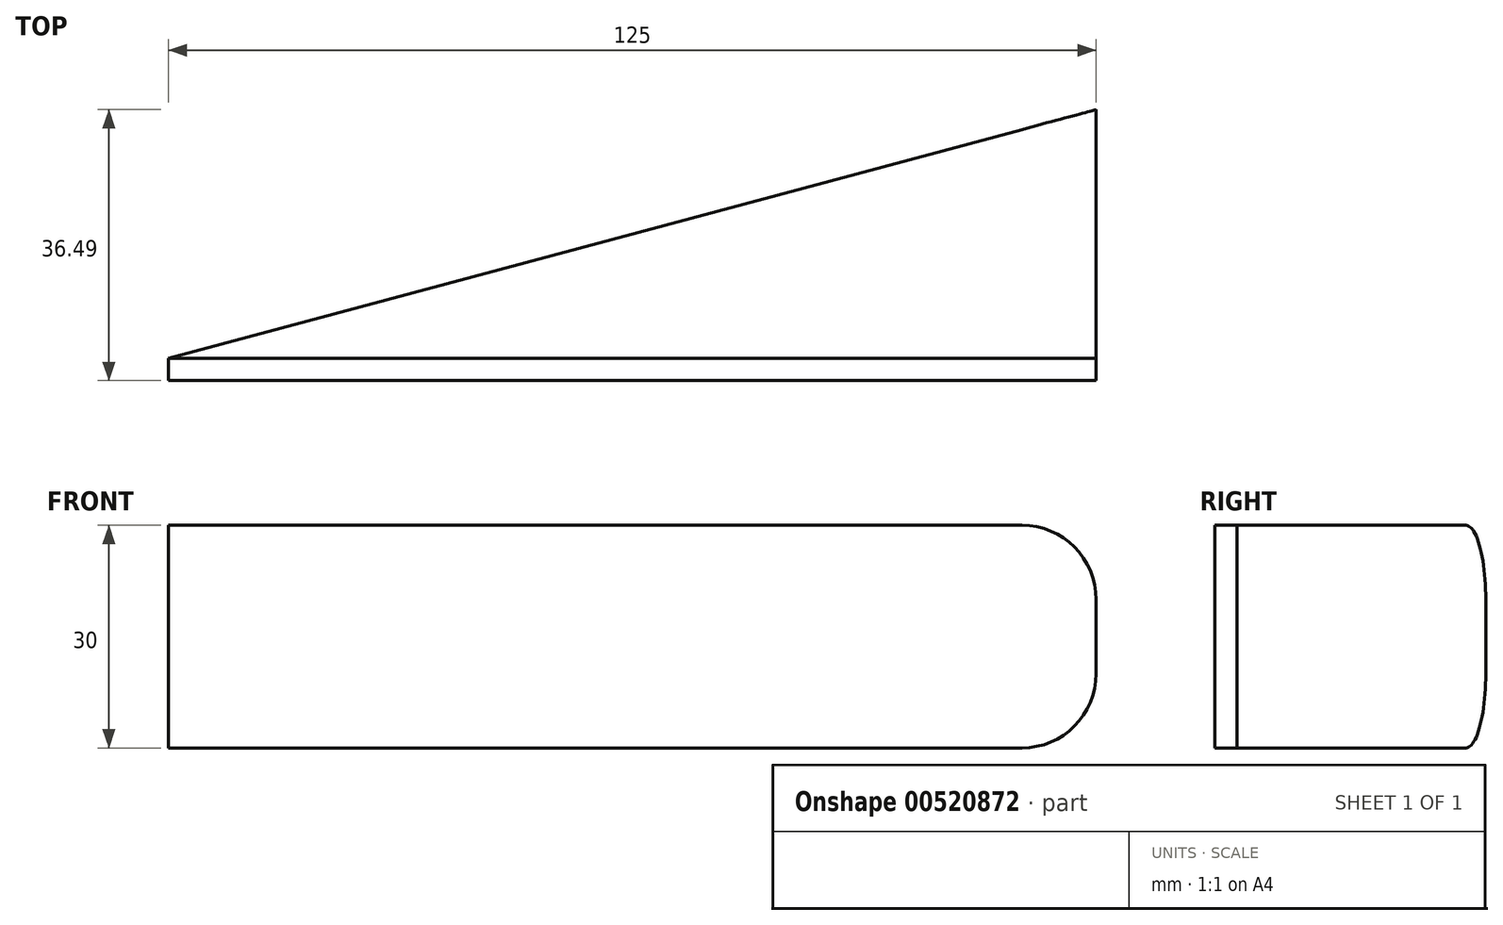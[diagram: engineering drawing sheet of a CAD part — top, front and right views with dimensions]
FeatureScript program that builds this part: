
annotation { "Feature Type Name" : "Feature", "Feature Type Description" : "" }
export const myFeature = defineFeature(function(context is Context, id is Id, definition is map)
    precondition{}
    {
        {
            var Q0;
            Q0=qCreatedBy(makeId("Top.planeOp"),FACE);
            var sketch = newSketch(context, id + "F0", { "sketchPlane" : qUnion([Q0])});
            skLineSegment(sketch, "E0", {"start": v(0, 0) * mm, "end": v(125, 0) * mm});
            skLineSegment(sketch, "E1", {"start": v(125, 0) * mm, "end": v(125, 33.5) * mm});
            skLineSegment(sketch, "E2", {"start": v(125, 33.5) * mm, "end": v(0, 0) * mm});
            skLineSegment(sketch, "E3.top", {"start": v(0, -3) * mm, "end": v(125, -3) * mm});
            skLineSegment(sketch, "E3.left", {"start": v(0, 0) * mm, "end": v(0, -3) * mm});
            skLineSegment(sketch, "E3.right", {"start": v(125, 0) * mm, "end": v(125, -3) * mm});
            skSolve(sketch);
        }
        {
            var Q0;
            Q0=makeQuery(id+"F0.imprint","IMPRINT",FACE,{"disambiguationData":[TD([[makeQuery(id+"F0.imprint","IMPRINT",EDGE,{"derivedFrom":sQuery(id+"F0.wireOp",EDGE,"E1")}),1.0]])]});
            extrude(context, id + "F1", {"entities" : qUnion([Q0]), "depth" : 30 * mm, "offsetDistance" : 25 * mm});
        }
        {
            var Q0;
            Q0=makeQuery(id+"F0.imprint","IMPRINT",FACE,{"disambiguationData":[TD([[makeQuery(id+"F0.imprint","IMPRINT",EDGE,{"derivedFrom":sQuery(id+"F0.wireOp",EDGE,"E0")}),-1.0]])]});
            extrude(context, id + "F2", {"entities" : qUnion([Q0]), "depth" : 30 * mm, "offsetDistance" : 25 * mm});
        }
        {
            var Q0;
            Q0=makeQuery(id+"F1.opExtrude","CAP_EDGE",EDGE,{"disambiguationData":[OSD([sQuery(id+"F0.wireOp",EDGE,"E1")])],"isStart":false});
            var Q1;
            Q1=makeQuery(id+"F2.opExtrude","CAP_EDGE",EDGE,{"disambiguationData":[OSD([sQuery(id+"F0.wireOp",EDGE,"E3.right")])],"isStart":false});
            fillet(context, id + "F3", {"entities" : qUnion([Q0, Q1]), "radius" : 10 * mm, "tangentPropagation" : true, "allowEdgeOverflow" : false});
        }
        {
            var Q0;
            Q0=makeQuery(id+"F1.opExtrude","CAP_EDGE",EDGE,{"disambiguationData":[OSD([sQuery(id+"F0.wireOp",EDGE,"E1")])],"isStart":true});
            fillet(context, id + "F4", {"entities" : qUnion([Q0]), "radius" : 10 * mm, "tangentPropagation" : true, "allowEdgeOverflow" : false});
        }
        {
            var Q0;
            Q0=makeQuery(id+"F2.opExtrude","CAP_EDGE",EDGE,{"disambiguationData":[OSD([sQuery(id+"F0.wireOp",EDGE,"E3.right")])],"isStart":true});
            fillet(context, id + "F5", {"entities" : qUnion([Q0]), "radius" : 10 * mm, "tangentPropagation" : true, "allowEdgeOverflow" : false});
        }
    });
